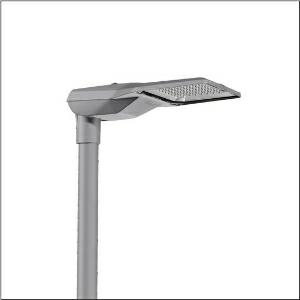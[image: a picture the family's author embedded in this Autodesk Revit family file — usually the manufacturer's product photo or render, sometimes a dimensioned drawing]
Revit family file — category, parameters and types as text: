
# Revit family: streetlight_sl_21_midi___stw1_0a_5xe3e43s08nb_fb33
name_source: partatom
category: Lighting Fixtures
units: mm (PartAtom-declared; Revit-internal decimal feet)

## family parameters
Cut with Voids When Loaded = No
Host = Face
Light Source = No
Part Type = Normal
Room Calculation Point = No
Round Connector Dimension = Use Diameter
Shared = No

## types (1)
- --- (1 x LED, 23710 lm, 151.2 W, 4000K)
    Apparent Load = 151 VA
    CIE Flux Codes = 39 75 98 100 100
    Color Rendering = 70
    Color Temperature = 4000K
    Default Elevation = 1800 mm
    Description = Streetlight SL 21 midi, mast luminaire, primary light control with lens, of PMMA, primary optical cover: cover, of toughened safety glass, transparent, light distribution: STW1.0a, light emission: direct distribution, primary light characteristic: asymmetric, installation type: side-entry, post-top, LED, High Power LED, rated luminous flux: 23.710lm, luminous efficacy: 157lm/W, light colour: 740, colour temperature: 4000K, control gear: D4i, control: overheat protection, constant luminous flux control, time-dependent luminous flux control, flexible luminous flux parameterisation, pre-setting: logarithmic dimming characteristic, mains connection: 230..240V, AC, 50/60Hz, start of lifetime: 151W, end of service life: 157W, reduction: 70W, luminaire housing, of diecast aluminium, powder-coated, SITECO metallic grey (DB 702S), corrosivity category C5 high according to DIN EN ISO 12944, please order mast flange separately, inclination adjustable: 0°, 5°, 10°, 15°, sealing non-destructively replaceable, multi-level sealing system, length: 644mm, width: 335mm, height: 110mm, mast flange for spigot size: 42mm (side-entry): 5XC10008XM4, 60/48mm (side-entry/post-top): 5XC10108XM2, 76/60mm (side-entry/post-top): 5XC10108XM1, mounting height: 4..8m, Smart Interface above, protection rating (complete): IP66, insulation class (complete): insulation class II (safety insulation), certification: CE, ENEC, ENEC+, VDE, impact resistance: IK10, permissible operating ambient temperature for outdoor applications: -40..+50°C, standard-compliant lighting for roads and squares, packaging unit: 1 piece

Light Distribution: STW1.0a
    Height = 111 mm
    Lamp = 1 x LED
    Lamp Light Flux = 23710 lm
    Lamp Power = 151.2 W
    Lamp count = 1
    Length = 644 mm
    Luminous efficacy = 157 lm/W
    Manufacturer = Siteco
    ModVariant = No
    Model = 5XE3E43S08NB
    Number of Poles = 1
    OnlyDefault = Yes
    Power Factor = 1
    Product Name = Streetlight SL 21 midi | STW1.0a
    Product group = mast luminaire | pylon top
    ProductGroupID = 6100
    Protection Class = Protection class II
    Protection Degree = IP 66
    RLX_Detail_Level = 1
    RLX_Emergency_Light_Flux = 0 lm
    RLX_Emergency_Type = 0
    RLX_Emergency_Type_DB = No
    RlxData = <blob elided: 27013 chars, md5=7281a5b7>
    Socket = socket
    Standby Power = 0 W
    System Light Flux = 23710 lm
    System Power = 151 W
    Type Comments = factory setting: luminous flux: 100 % | dim-lin: 254 | 802 mA
    Type Image = l_1004302.jpg
    URL = http://relux.com
    VarID = @adj_169125
    Voltage = 0 V
    Weight = 0.00 kg
    Width = 336 mm

## geometry (parser evidence)
native form markers: Blend x4, Sweep x11
no freeform markers — native parametric forms only
